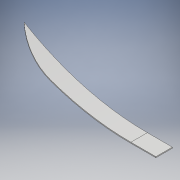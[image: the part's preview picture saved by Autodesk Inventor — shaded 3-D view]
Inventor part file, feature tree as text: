
AUTODESK INVENTOR PART (.ipt)
format: ipt  version: 2018 (Build 220112000, 112)  size: 133,632 bytes
history: native  units: mm
features: other x5, projected_geometry x2, extrude x1, sketch x1
ambient origin geometry x8: Origin, YZ Plane, XZ Plane, XY Plane, X Axis, Y Axis, Z Axis, Center Point
bodies: Body1 (feature_tree)
feature tree (9):
  other  "endplate_ver2.ipt"
  extrude  "押し出し1"  Depth=10.0mm
  other  "面を削除1"
  other  "ソリッド2::endplate_ver2.ipt"
  other  "TaggingFeature1"
  sketch  "スケッチ1"
  projected_geometry  "投影ループ1"
  projected_geometry  "投影ループ2"
  other  "ソリッド1"
